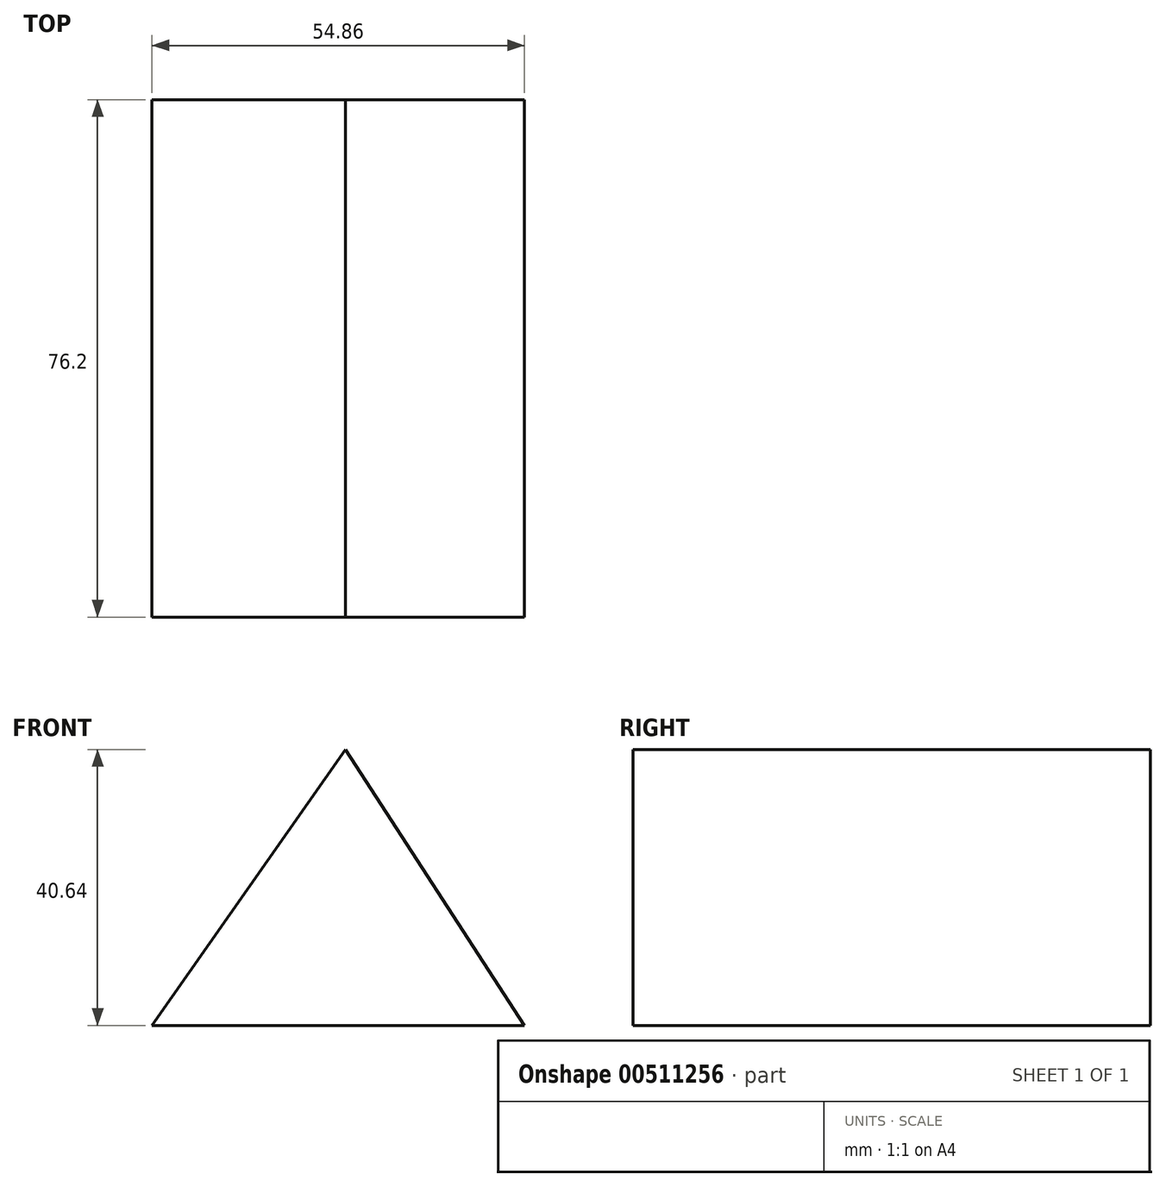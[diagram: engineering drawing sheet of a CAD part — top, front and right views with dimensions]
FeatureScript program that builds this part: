
annotation { "Feature Type Name" : "Feature", "Feature Type Description" : "" }
export const myFeature = defineFeature(function(context is Context, id is Id, definition is map)
    precondition{}
    {
        {
            var Q0;
            Q0=qCreatedBy(makeId("Front.planeOp"),FACE);
            var sketch = newSketch(context, id + "F0", { "sketchPlane" : qUnion([Q0])});
            skLineSegment(sketch, "E0", {"start": v(-28.5, 0) * mm, "end": v(26.36, 0) * mm});
            skLineSegment(sketch, "E1", {"start": v(-28.5, 0) * mm, "end": v(0, 40.64) * mm});
            skLineSegment(sketch, "E2", {"start": v(0, 40.64) * mm, "end": v(26.36, 0) * mm});
            skLineSegment(sketch, "E3", {"start": v(0, 40.64) * mm, "end": v(0, 0) * mm});
            skSolve(sketch);
        }
        {
            var Q0;
            Q0 = qSketchRegion(id + "F0", true);
            extrude(context, id + "F1", {"entities" : qUnion([Q0]), "depth" : 76.2 * mm});
        }
    });
